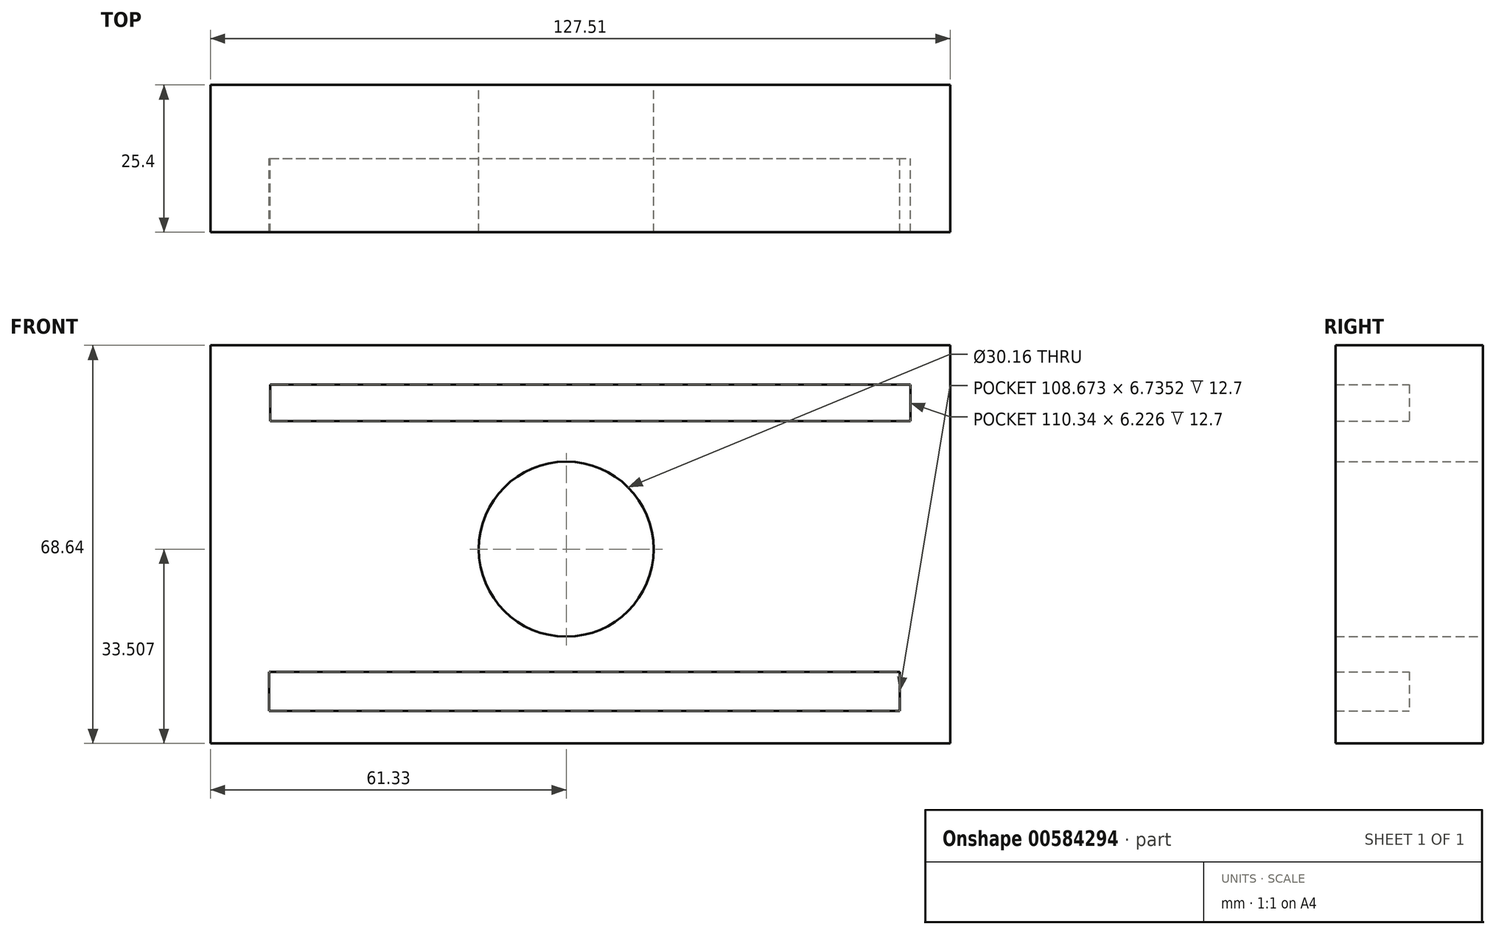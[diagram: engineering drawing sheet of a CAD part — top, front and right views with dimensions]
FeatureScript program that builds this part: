
annotation { "Feature Type Name" : "Feature", "Feature Type Description" : "" }
export const myFeature = defineFeature(function(context is Context, id is Id, definition is map)
    precondition{}
    {
        {
            var Q0;
            Q0=qCreatedBy(makeId("Front.planeOp"),FACE);
            var sketch = newSketch(context, id + "F0", { "sketchPlane" : qUnion([Q0])});
            skLineSegment(sketch, "E0.bottom", {"start": v(-61.33, 48.64) * mm, "end": v(66.18, 48.64) * mm});
            skLineSegment(sketch, "E0.top", {"start": v(-61.33, -20) * mm, "end": v(66.18, -20) * mm});
            skLineSegment(sketch, "E0.left", {"start": v(-61.33, 48.64) * mm, "end": v(-61.33, -20) * mm});
            skLineSegment(sketch, "E0.right", {"start": v(66.18, 48.64) * mm, "end": v(66.18, -20) * mm});
            skCircle(sketch, "E1", {"center": v(0, 13.5) * mm, "radius": 15.08 * mm});
            skLineSegment(sketch, "E2", {"start": v(0.31, 28.59) * mm, "end": v(-61.33, 28.59) * mm});
            skLineSegment(sketch, "E3", {"start": v(-61.33, 28.59) * mm, "end": v(66.18, 28.59) * mm});
            skLineSegment(sketch, "E4", {"start": v(-61.33, -1.58) * mm, "end": v(0, -1.58) * mm});
            skLineSegment(sketch, "E5", {"start": v(0, -1.58) * mm, "end": v(66.18, -1.58) * mm});
            skLineSegment(sketch, "E6.bottom", {"start": v(-51.19, -7.63) * mm, "end": v(57.49, -7.63) * mm});
            skLineSegment(sketch, "E6.top", {"start": v(-51.19, -14.37) * mm, "end": v(57.49, -14.37) * mm});
            skLineSegment(sketch, "E6.left", {"start": v(-51.19, -7.63) * mm, "end": v(-51.19, -14.37) * mm});
            skLineSegment(sketch, "E6.right", {"start": v(57.49, -7.63) * mm, "end": v(57.49, -14.37) * mm});
            skLineSegment(sketch, "E7.bottom", {"start": v(-51.19, -14.37) * mm, "end": v(-51.19, -14.37) * mm});
            skLineSegment(sketch, "E7.top", {"start": v(-51.19, -14.37) * mm, "end": v(-51.19, -14.37) * mm});
            skLineSegment(sketch, "E7.left", {"start": v(-51.19, -14.37) * mm, "end": v(-51.19, -14.37) * mm});
            skLineSegment(sketch, "E7.right", {"start": v(-51.19, -14.37) * mm, "end": v(-51.19, -14.37) * mm});
            skLineSegment(sketch, "E8.bottom", {"start": v(-51.01, 41.84) * mm, "end": v(59.33, 41.84) * mm});
            skLineSegment(sketch, "E8.top", {"start": v(-51.01, 35.62) * mm, "end": v(59.33, 35.62) * mm});
            skLineSegment(sketch, "E8.left", {"start": v(-51.01, 41.84) * mm, "end": v(-51.01, 35.62) * mm});
            skLineSegment(sketch, "E8.right", {"start": v(59.33, 41.84) * mm, "end": v(59.33, 35.62) * mm});
            skSolve(sketch);
        }
        {
            var Q0;
            {var subQ5=sQuery(id+"F0.wireOp",EDGE,"E0.bottom");Q0=makeQuery(id+"F0.imprint","IMPRINT",FACE,{"disambiguationData":[TD([[makeQuery(id+"F0.imprint","IMPRINT",EDGE,{"derivedFrom":subQ5}),-1.0]])]});}
            var Q1;
            {var subQ1=sQuery(id+"F0.wireOp",EDGE,"E0.top");Q1=makeQuery(id+"F0.imprint","IMPRINT",FACE,{"disambiguationData":[TD([[makeQuery(id+"F0.imprint","IMPRINT",EDGE,{"derivedFrom":subQ1}),1.0]])]});}
            var Q2;
            {var subQ3=sQuery(id+"F0.wireOp",EDGE,"E4");Q2=makeQuery(id+"F0.imprint","IMPRINT",FACE,{"disambiguationData":[TD([[makeQuery(id+"F0.imprint","IMPRINT",EDGE,{"derivedFrom":subQ3}),1.0]])]});}
            var Q3;
            {var subQ3=sQuery(id+"F0.wireOp",EDGE,"E5");Q3=makeQuery(id+"F0.imprint","IMPRINT",FACE,{"disambiguationData":[TD([[makeQuery(id+"F0.imprint","IMPRINT",EDGE,{"derivedFrom":subQ3}),1.0]])]});}
            extrude(context, id + "F1", {"entities" : qUnion([Q0, Q1, Q2, Q3]), "endBound" : BoundingType.SYMMETRIC, "depth" : 25.4 * mm, "offsetDistance" : 25.4 * mm});
        }
        {
            var Q0;
            Q0=makeQuery(id+"F0.imprint","IMPRINT",FACE,{"disambiguationData":[TD([[makeQuery(id+"F0.imprint","IMPRINT",EDGE,{"derivedFrom":sQuery(id+"F0.wireOp",EDGE,"E8.bottom")}),-1.0]])]});
            var Q1;
            Q1=makeQuery(id+"F0.imprint","IMPRINT",FACE,{"disambiguationData":[TD([[makeQuery(id+"F0.imprint","IMPRINT",EDGE,{"derivedFrom":sQuery(id+"F0.wireOp",EDGE,"E6.bottom")}),-1.0]])]});
            extrude(context, id + "F2", {"entities" : qUnion([Q0, Q1]), "operationType" : NewBodyOperationType.ADD, "oppositeDirection" : true, "depth" : 12.7 * mm, "offsetDistance" : 25.4 * mm});
        }
        {
            var Q0;
            {var subQ0=sQuery(id+"F0.wireOp",EDGE,"E1");var subQ2=sQuery(id+"F0.wireOp",EDGE,"E3");var subQ3=makeQuery(id+"F0.imprint","INTERSECT",VERTEX,{"disambiguationData":[OD(0.0)],"derivedFrom":[subQ0,subQ2]});Q0=makeQuery(id+"F0.imprint","IMPRINT",FACE,{"disambiguationData":[TD([[makeQuery(id+"F0.imprint","IMPRINT",EDGE,{"disambiguationData":[TD([[subQ3,-1.0]])],"derivedFrom":subQ2}),-1.0]])]});}
            extrude(context, id + "F3", {"entities" : qUnion([Q0]), "operationType" : NewBodyOperationType.ADD, "oppositeDirection" : true, "depth" : 12.7 * mm, "offsetDistance" : 25.4 * mm});
        }
    });
